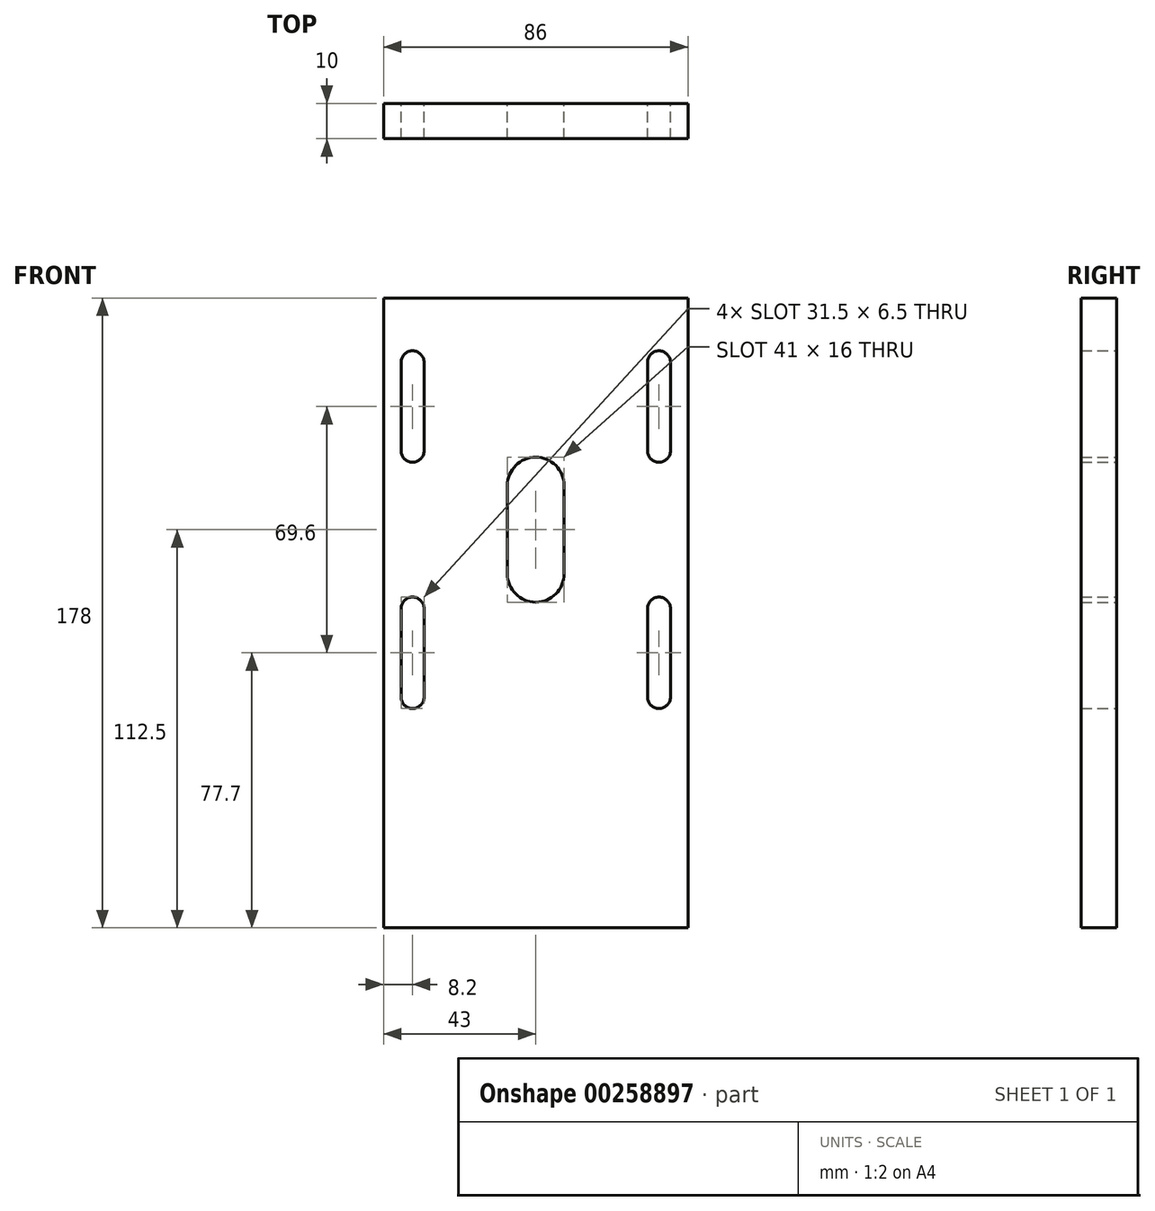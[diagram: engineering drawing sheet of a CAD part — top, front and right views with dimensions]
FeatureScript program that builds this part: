
annotation { "Feature Type Name" : "Feature", "Feature Type Description" : "" }
export const myFeature = defineFeature(function(context is Context, id is Id, definition is map)
    precondition{}
    {
        {
            var Q0;
            Q0=qCreatedBy(makeId("Front.planeOp"),FACE);
            var sketch = newSketch(context, id + "F0", { "sketchPlane" : qUnion([Q0])});
            skLineSegment(sketch, "E0", {"start": v(-43, 0) * mm, "end": v(-43, 63) * mm});
            skLineSegment(sketch, "E1", {"start": v(-43, 63) * mm, "end": v(43, 63) * mm});
            skLineSegment(sketch, "E2", {"start": v(43, 63) * mm, "end": v(43, 0) * mm});
            skLineSegment(sketch, "E3", {"start": v(43, 0) * mm, "end": v(43, -115) * mm});
            skLineSegment(sketch, "E4", {"start": v(43, -115) * mm, "end": v(-43, -115) * mm});
            skLineSegment(sketch, "E5", {"start": v(-43, -115) * mm, "end": v(-43, 0) * mm});
            skCircle(sketch, "E6", {"center": v(0, 0) * mm, "radius": 7 * mm, "construction": true});
            skCircle(sketch, "E7", {"center": v(0, -87) * mm, "radius": 6 * mm, "construction": true});
            skCircle(sketch, "E8", {"center": v(-34.8, 34.8) * mm, "radius": 3.25 * mm, "construction": true});
            skLineSegment(sketch, "E9", {"start": v(-31.55, 34.8) * mm, "end": v(-31.55, 44.8) * mm});
            skLineSegment(sketch, "E10", {"start": v(-38.05, 44.8) * mm, "end": v(-38.05, 34.8) * mm});
            skArc(sketch, "E11", {"start": v(-38.05, 44.8) * mm, "mid": v(-34.8, 48.05) * mm, "end": v(-31.55, 44.8) * mm});
            skLineSegment(sketch, "E12", {"start": v(-38.05, 34.8) * mm, "end": v(-38.05, 19.8) * mm});
            skLineSegment(sketch, "E13", {"start": v(-31.55, 34.8) * mm, "end": v(-31.55, 19.8) * mm});
            skArc(sketch, "E14", {"start": v(-38.05, 19.8) * mm, "mid": v(-34.8, 16.55) * mm, "end": v(-31.55, 19.8) * mm});
            skCircle(sketch, "E15.0.1.0", {"center": v(-34.8, -34.8) * mm, "radius": 3.25 * mm, "construction": true});
            skArc(sketch, "E15.0.1.1", {"start": v(-38.05, -24.8) * mm, "mid": v(-34.8, -21.55) * mm, "end": v(-31.55, -24.8) * mm});
            skLineSegment(sketch, "E15.0.1.2", {"start": v(-31.55, -34.8) * mm, "end": v(-31.55, -49.8) * mm});
            skLineSegment(sketch, "E15.0.1.3", {"start": v(-38.05, -34.8) * mm, "end": v(-38.05, -49.8) * mm});
            skArc(sketch, "E15.0.1.4", {"start": v(-38.05, -49.8) * mm, "mid": v(-34.8, -53.05) * mm, "end": v(-31.55, -49.8) * mm});
            skLineSegment(sketch, "E15.0.1.5", {"start": v(-31.55, -34.8) * mm, "end": v(-31.55, -24.8) * mm});
            skLineSegment(sketch, "E15.0.1.6", {"start": v(-38.05, -24.8) * mm, "end": v(-38.05, -34.8) * mm});
            skCircle(sketch, "E15.1.0.0", {"center": v(34.8, 34.8) * mm, "radius": 3.25 * mm, "construction": true});
            skArc(sketch, "E15.1.0.1", {"start": v(31.55, 44.8) * mm, "mid": v(34.8, 48.05) * mm, "end": v(38.05, 44.8) * mm});
            skLineSegment(sketch, "E15.1.0.2", {"start": v(38.05, 34.8) * mm, "end": v(38.05, 19.8) * mm});
            skLineSegment(sketch, "E15.1.0.3", {"start": v(31.55, 34.8) * mm, "end": v(31.55, 19.8) * mm});
            skArc(sketch, "E15.1.0.4", {"start": v(31.55, 19.8) * mm, "mid": v(34.8, 16.55) * mm, "end": v(38.05, 19.8) * mm});
            skLineSegment(sketch, "E15.1.0.5", {"start": v(38.05, 34.8) * mm, "end": v(38.05, 44.8) * mm});
            skLineSegment(sketch, "E15.1.0.6", {"start": v(31.55, 44.8) * mm, "end": v(31.55, 34.8) * mm});
            skCircle(sketch, "E15.1.1.0", {"center": v(34.8, -34.8) * mm, "radius": 3.25 * mm, "construction": true});
            skArc(sketch, "E15.1.1.1", {"start": v(31.55, -24.8) * mm, "mid": v(34.8, -21.55) * mm, "end": v(38.05, -24.8) * mm});
            skLineSegment(sketch, "E15.1.1.2", {"start": v(38.05, -34.8) * mm, "end": v(38.05, -49.8) * mm});
            skLineSegment(sketch, "E15.1.1.3", {"start": v(31.55, -34.8) * mm, "end": v(31.55, -49.8) * mm});
            skArc(sketch, "E15.1.1.4", {"start": v(31.55, -49.8) * mm, "mid": v(34.8, -53.05) * mm, "end": v(38.05, -49.8) * mm});
            skLineSegment(sketch, "E15.1.1.5", {"start": v(38.05, -34.8) * mm, "end": v(38.05, -24.8) * mm});
            skLineSegment(sketch, "E15.1.1.6", {"start": v(31.55, -24.8) * mm, "end": v(31.55, -34.8) * mm});
            skLineSegment(sketch, "E15.direction1", {"start": v(-38.05, 19.8) * mm, "end": v(31.55, 19.8) * mm, "construction": true});
            skLineSegment(sketch, "E15.direction2", {"start": v(-38.05, 19.8) * mm, "end": v(-38.05, -49.8) * mm, "construction": true});
            skCircle(sketch, "E16", {"center": v(0, 0) * mm, "radius": 8 * mm, "construction": true});
            skLineSegment(sketch, "E17", {"start": v(8, 0) * mm, "end": v(8, 10) * mm});
            skLineSegment(sketch, "E18", {"start": v(-8, 0) * mm, "end": v(-8, 10) * mm});
            skArc(sketch, "E19", {"start": v(-8, 10) * mm, "mid": v(0, 18) * mm, "end": v(8, 10) * mm});
            skLineSegment(sketch, "E20", {"start": v(8, 0) * mm, "end": v(8, -15) * mm});
            skLineSegment(sketch, "E21", {"start": v(-8, 0) * mm, "end": v(-8, -15) * mm});
            skArc(sketch, "E22", {"start": v(8, -15) * mm, "mid": v(0, -23) * mm, "end": v(-8, -15) * mm});
            skSolve(sketch);
        }
        {
            var Q0;
            Q0=makeQuery(id+"F0.imprint","IMPRINT",FACE,{"disambiguationData":[TD([[makeQuery(id+"F0.imprint","IMPRINT",EDGE,{"derivedFrom":sQuery(id+"F0.wireOp",EDGE,"E0")}),-1.0]])]});
            extrude(context, id + "F1", {"entities" : qUnion([Q0]), "depth" : 10 * mm});
        }
    });
